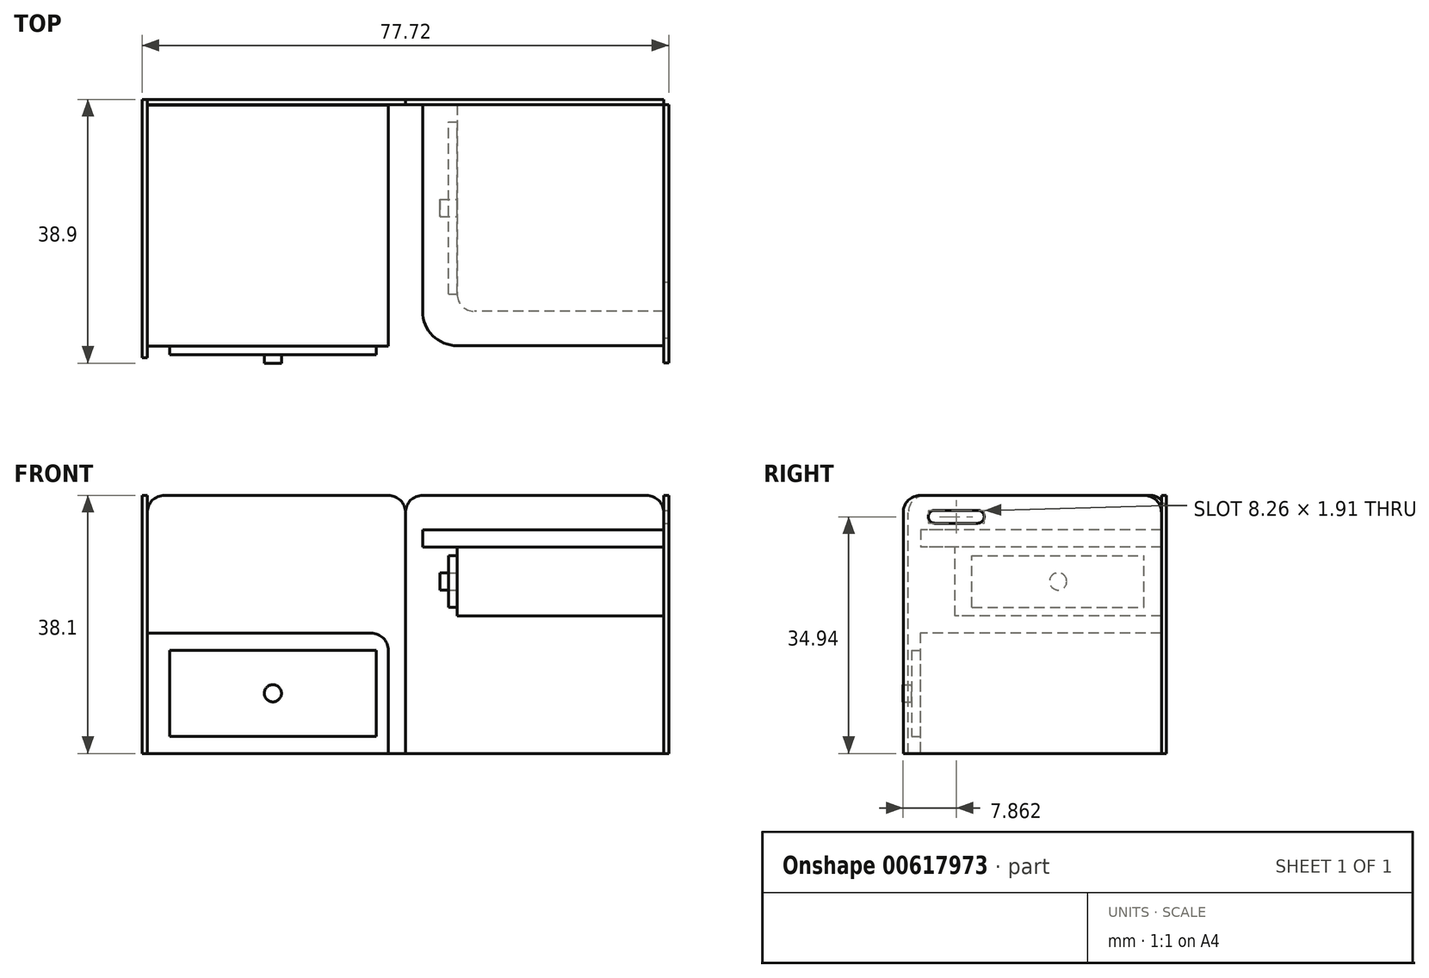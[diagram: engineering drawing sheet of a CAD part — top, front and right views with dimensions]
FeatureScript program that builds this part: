
annotation { "Feature Type Name" : "Feature", "Feature Type Description" : "" }
export const myFeature = defineFeature(function(context is Context, id is Id, definition is map)
    precondition{}
    {
        {
            var Q0;
            Q0=qCreatedBy(makeId("Right.planeOp"),FACE);
            var sketch = newSketch(context, id + "F0", { "sketchPlane" : qUnion([Q0])});
            skLineSegment(sketch, "E0.bottom", {"start": v(0, 0) * mm, "end": v(-38.1, 0) * mm});
            skLineSegment(sketch, "E0.top", {"start": v(0, 38.1) * mm, "end": v(-38.1, 38.1) * mm});
            skLineSegment(sketch, "E0.left", {"start": v(0, 0) * mm, "end": v(0, 38.1) * mm});
            skLineSegment(sketch, "E0.right", {"start": v(-38.1, 0) * mm, "end": v(-38.1, 38.1) * mm});
            skSolve(sketch);
        }
        {
            var Q0;
            Q0=qCreatedBy(makeId("Front.planeOp"),FACE);
            var sketch = newSketch(context, id + "F1", { "sketchPlane" : qUnion([Q0])});
            skLineSegment(sketch, "E1.0", {"start": v(0, 0) * mm, "end": v(0, 38.1) * mm});
            skLineSegment(sketch, "E2.bottom", {"start": v(0, 38.1) * mm, "end": v(38.1, 38.1) * mm});
            skLineSegment(sketch, "E2.top", {"start": v(0, 0) * mm, "end": v(38.1, 0) * mm});
            skLineSegment(sketch, "E2.left", {"start": v(0, 38.1) * mm, "end": v(0, 0) * mm});
            skLineSegment(sketch, "E2.right", {"start": v(38.1, 38.1) * mm, "end": v(38.1, 0) * mm});
            skLineSegment(sketch, "E3.bottom", {"start": v(38.1, 38.1) * mm, "end": v(76.2, 38.1) * mm});
            skLineSegment(sketch, "E3.top", {"start": v(38.1, 0) * mm, "end": v(76.2, 0) * mm});
            skLineSegment(sketch, "E3.right", {"start": v(76.2, 38.1) * mm, "end": v(76.2, 0) * mm});
            skSolve(sketch);
        }
        {
            var Q0;
            Q0=makeQuery(id+"F0.imprint","IMPRINT",FACE,{"disambiguationData":[TD([[makeQuery(id+"F0.imprint","IMPRINT",EDGE,{"derivedFrom":sQuery(id+"F0.wireOp",EDGE,"E0.bottom")}),-1.0]])]});
            extrude(context, id + "F2", {"entities" : qUnion([Q0]), "oppositeDirection" : true, "depth" : 0.76 * mm, "offsetDistance" : 25.4 * mm});
        }
        {
            var Q0;
            Q0=makeQuery(id+"F1.imprint","IMPRINT",FACE,{"disambiguationData":[TD([[makeQuery(id+"F1.imprint","IMPRINT",EDGE,{"derivedFrom":sQuery(id+"F1.wireOp",EDGE,"E2.bottom")}),-1.0]])]});
            extrude(context, id + "F3", {"entities" : qUnion([Q0]), "depth" : 0.76 * mm, "offsetDistance" : 25.4 * mm});
        }
        {
            var Q0;
            Q0=qCreatedBy(makeId("Top.planeOp"),FACE);
            var sketch = newSketch(context, id + "F4", { "sketchPlane" : qUnion([Q0])});
            skPoint(sketch, "E4.0", {"position": v(0, -0.8) * mm});
            skLineSegment(sketch, "E5.bottom", {"start": v(0, -0.8) * mm, "end": v(35.56, -0.8) * mm});
            skLineSegment(sketch, "E5.top", {"start": v(0, -36.36) * mm, "end": v(35.56, -36.36) * mm});
            skLineSegment(sketch, "E5.left", {"start": v(0, -0.8) * mm, "end": v(0, -36.36) * mm});
            skLineSegment(sketch, "E5.right", {"start": v(35.56, -0.8) * mm, "end": v(35.56, -36.36) * mm});
            skSolve(sketch);
        }
        {
            var Q0;
            Q0=makeQuery(id+"F4.imprint","IMPRINT",FACE,{"disambiguationData":[TD([[makeQuery(id+"F4.imprint","IMPRINT",EDGE,{"derivedFrom":sQuery(id+"F4.wireOp",EDGE,"E5.bottom")}),-1.0]])]});
            extrude(context, id + "F5", {"entities" : qUnion([Q0]), "depth" : 17.78 * mm});
        }
        {
            var Q0;
            Q0=makeQuery(id+"F5.opExtrude","CAP_FACE",FACE,{"disambiguationData":[OSD([sQuery(id+"F4.wireOp",EDGE,"E5.bottom"),sQuery(id+"F4.wireOp",EDGE,"E5.top"),sQuery(id+"F4.wireOp",EDGE,"E5.left"),sQuery(id+"F4.wireOp",EDGE,"E5.right")])],"isStart":false});
            cPlane(context, id + "F6", {"entities" : qUnion([Q0]), "cplaneType" : CPlaneType.OFFSET, "offset" : 12.7 * mm, "width" : 152.4 * mm, "height" : 152.4 * mm});
        }
        {
            var Q0;
            Q0=qCreatedBy(id+"F6.planeOp",FACE);
            var sketch = newSketch(context, id + "F7", { "sketchPlane" : qUnion([Q0])});
            skLineSegment(sketch, "E6.bottom", {"start": v(76.2, -0.76) * mm, "end": v(40.64, -0.76) * mm});
            skLineSegment(sketch, "E6.top", {"start": v(76.2, -36.32) * mm, "end": v(40.64, -36.32) * mm});
            skLineSegment(sketch, "E6.left", {"start": v(76.2, -0.76) * mm, "end": v(76.2, -36.32) * mm});
            skLineSegment(sketch, "E6.right", {"start": v(40.64, -0.76) * mm, "end": v(40.64, -36.32) * mm});
            skSolve(sketch);
        }
        {
            var Q0;
            Q0=qCreatedBy(id+"F6.planeOp",FACE);
            var sketch = newSketch(context, id + "F8", { "sketchPlane" : qUnion([Q0])});
            skLineSegment(sketch, "E7.bottom", {"start": v(76.2, -0.76) * mm, "end": v(45.72, -0.76) * mm});
            skLineSegment(sketch, "E7.top", {"start": v(76.2, -31.24) * mm, "end": v(45.72, -31.24) * mm});
            skLineSegment(sketch, "E7.left", {"start": v(76.2, -0.76) * mm, "end": v(76.2, -31.24) * mm});
            skLineSegment(sketch, "E7.right", {"start": v(45.72, -0.76) * mm, "end": v(45.72, -31.24) * mm});
            skSolve(sketch);
        }
        {
            var Q0;
            Q0=makeQuery(id+"F8.imprint","IMPRINT",FACE,{"disambiguationData":[TD([[makeQuery(id+"F8.imprint","IMPRINT",EDGE,{"derivedFrom":sQuery(id+"F8.wireOp",EDGE,"E7.bottom")}),1.0]])]});
            extrude(context, id + "F9", {"entities" : qUnion([Q0]), "oppositeDirection" : true, "depth" : 10.16 * mm});
        }
        {
            var Q0;
            Q0=qSketchRegion(id+"F7",true);
            extrude(context, id + "F10", {"entities" : qUnion([Q0]), "depth" : 2.54 * mm});
        }
        {
            var Q0;
            Q0=makeQuery(id+"F5.opExtrude","SWEPT_FACE",FACE,{"disambiguationData":[OSD([sQuery(id+"F4.wireOp",EDGE,"E5.top")])]});
            var sketch = newSketch(context, id + "F11", { "sketchPlane" : qUnion([Q0])});
            skLineSegment(sketch, "E8.0", {"start": v(35.56, 17.78) * mm, "end": v(35.56, 0) * mm});
            skLineSegment(sketch, "E9.0.2", {"start": v(35.56, 17.78) * mm, "end": v(0, 17.78) * mm});
            skLineSegment(sketch, "E9.0.3", {"start": v(0, 17.78) * mm, "end": v(0, 0) * mm});
            skLineSegment(sketch, "E10.bottom", {"start": v(33.78, 15.24) * mm, "end": v(3.3, 15.24) * mm});
            skLineSegment(sketch, "E10.top", {"start": v(33.78, 2.54) * mm, "end": v(3.3, 2.54) * mm});
            skLineSegment(sketch, "E10.left", {"start": v(33.78, 15.24) * mm, "end": v(33.78, 2.54) * mm});
            skLineSegment(sketch, "E10.right", {"start": v(3.3, 15.24) * mm, "end": v(3.3, 2.54) * mm});
            skPoint(sketch, "E10.middle", {"position": v(18.54, 8.9) * mm});
            skSolve(sketch);
        }
        {
            var Q0;
            Q0=makeQuery(id+"F11.imprint","IMPRINT",FACE,{"disambiguationData":[TD([[makeQuery(id+"F11.imprint","IMPRINT",EDGE,{"derivedFrom":sQuery(id+"F11.wireOp",EDGE,"E10.bottom")}),1.0]])]});
            extrude(context, id + "F12", {"entities" : qUnion([Q0]), "depth" : 1.27 * mm});
        }
        {
            var Q0;
            Q0=makeQuery(id+"F12.opExtrude","CAP_FACE",FACE,{"disambiguationData":[OSD([sQuery(id+"F11.wireOp",EDGE,"E10.bottom"),sQuery(id+"F11.wireOp",EDGE,"E10.top"),sQuery(id+"F11.wireOp",EDGE,"E10.left"),sQuery(id+"F11.wireOp",EDGE,"E10.right")])],"isStart":false});
            var sketch = newSketch(context, id + "F13", { "sketchPlane" : qUnion([Q0])});
            skCircle(sketch, "E11", {"center": v(18.54, 8.89) * mm, "radius": 1.27 * mm});
            skSolve(sketch);
        }
        {
            var Q0;
            Q0=makeQuery(id+"F13.imprint","IMPRINT",FACE,{"disambiguationData":[TD([[makeQuery(id+"F13.imprint","IMPRINT",EDGE,{"derivedFrom":sQuery(id+"F13.wireOp",EDGE,"E11")}),1.0]])]});
            extrude(context, id + "F14", {"entities" : qUnion([Q0]), "depth" : 1.27 * mm});
        }
        {
            var Q0;
            Q0=makeQuery(id+"F9.opExtrude","SWEPT_FACE",FACE,{"disambiguationData":[OSD([sQuery(id+"F8.wireOp",EDGE,"E7.right")])]});
            var sketch = newSketch(context, id + "F15", { "sketchPlane" : qUnion([Q0])});
            skLineSegment(sketch, "E12.bottom", {"start": v(28.7, 21.59) * mm, "end": v(3.3, 21.59) * mm});
            skLineSegment(sketch, "E12.top", {"start": v(28.7, 29.2) * mm, "end": v(3.3, 29.2) * mm});
            skLineSegment(sketch, "E12.left", {"start": v(28.7, 21.59) * mm, "end": v(28.7, 29.2) * mm});
            skLineSegment(sketch, "E12.right", {"start": v(3.3, 21.59) * mm, "end": v(3.3, 29.2) * mm});
            skPoint(sketch, "E12.middle", {"position": v(16, 25.4) * mm});
            skSolve(sketch);
        }
        {
            var Q0;
            Q0=makeQuery(id+"F15.imprint","IMPRINT",FACE,{"disambiguationData":[TD([[makeQuery(id+"F15.imprint","IMPRINT",EDGE,{"derivedFrom":sQuery(id+"F15.wireOp",EDGE,"E12.bottom")}),1.0]])]});
            var sketch = newSketch(context, id + "F16", { "sketchPlane" : qUnion([Q0])});
            skCircle(sketch, "E13", {"center": v(16, 25.4) * mm, "radius": 1.27 * mm});
            skSolve(sketch);
        }
        {
            var Q0;
            Q0=makeQuery(id+"F16.imprint","IMPRINT",FACE,{"disambiguationData":[TD([[makeQuery(id+"F16.imprint","IMPRINT",EDGE,{"derivedFrom":sQuery(id+"F16.wireOp",EDGE,"E13")}),1.0]])]});
            extrude(context, id + "F17", {"entities" : qUnion([Q0]), "depth" : 2.54 * mm});
        }
        {
            var Q0;
            Q0=makeQuery(id+"F15.imprint","IMPRINT",FACE,{"disambiguationData":[TD([[makeQuery(id+"F15.imprint","IMPRINT",EDGE,{"derivedFrom":sQuery(id+"F15.wireOp",EDGE,"E12.bottom")}),-1.0]])]});
            extrude(context, id + "F18", {"entities" : qUnion([Q0]), "depth" : 1.27 * mm});
        }
        {
            var Q0;
            Q0=makeQuery(id+"F2.opExtrude","SWEPT_EDGE",EDGE,{"disambiguationData":[OSD([sQuery(id+"F0.wireOp",EDGE,"E0.top"),sQuery(id+"F0.wireOp",EDGE,"E0.right")])]});
            var Q1;
            Q1=makeQuery(id+"F2.opExtrude","SWEPT_EDGE",EDGE,{"disambiguationData":[OSD([sQuery(id+"F0.wireOp",EDGE,"E0.top"),sQuery(id+"F0.wireOp",EDGE,"E0.left")])]});
            var Q2;
            Q2=makeQuery(id+"F3.opExtrude","SWEPT_EDGE",EDGE,{"disambiguationData":[OSD([sQuery(id+"FI0QwBpxzJms6q6_1.wireOp",EDGE,"EPlBsMqQ-QzQ8-VdCQ-xvKd-hzmvY7jMW2L1.bottom"),sQuery(id+"FI0QwBpxzJms6q6_1.wireOp",EDGE,"EPlBsMqQ-QzQ8-VdCQ-xvKd-hzmvY7jMW2L1.right")])]});
            var Q3;
            Q3=makeQuery(id+"FcK2yJQiMoCniT7_2.opExtrude","SWEPT_EDGE",EDGE,{"disambiguationData":[OSD([sQuery(id+"FKOlXeHhfTV6Gp4_1.wireOp",EDGE,"gBm9quYi-xdeT-jJYe-hTa2-NPwO5Kq9pGmv.bottom"),sQuery(id+"FKOlXeHhfTV6Gp4_1.wireOp",EDGE,"gBm9quYi-xdeT-jJYe-hTa2-NPwO5Kq9pGmv.right")])]});
            var Q4;
            Q4=makeQuery(id+"FcK2yJQiMoCniT7_2.opExtrude","SWEPT_EDGE",EDGE,{"disambiguationData":[OSD([sQuery(id+"FKOlXeHhfTV6Gp4_1.wireOp",EDGE,"gBm9quYi-xdeT-jJYe-hTa2-NPwO5Kq9pGmv.bottom"),sQuery(id+"FKOlXeHhfTV6Gp4_1.wireOp",EDGE,"gBm9quYi-xdeT-jJYe-hTa2-NPwO5Kq9pGmv.left")])]});
            var Q5;
            Q5=makeQuery(id+"F3.opExtrude","SWEPT_EDGE",EDGE,{"disambiguationData":[OSD([sQuery(id+"F1.wireOp",EDGE,"E3.bottom"),sQuery(id+"F1.wireOp",EDGE,"E3.right")])]});
            var Q6;
            Q6=makeQuery(id+"F3.opExtrude","SWEPT_EDGE",EDGE,{"disambiguationData":[OSD([sQuery(id+"F1.wireOp",EDGE,"E2.bottom"),sQuery(id+"F1.wireOp",EDGE,"E2.left")])]});
            fillet(context, id + "F19", {"entities" : qUnion([Q0, Q1, Q2, Q3, Q4, Q5, Q6]), "radius" : 2.54 * mm, "tangentPropagation" : true, "allowEdgeOverflow" : false});
        }
        {
            var Q0;
            Q0=makeQuery(id+"F10.opExtrude","SWEPT_EDGE",EDGE,{"disambiguationData":[OSD([sQuery(id+"F7.wireOp",EDGE,"E6.top"),sQuery(id+"F7.wireOp",EDGE,"E6.right")])]});
            fillet(context, id + "F20", {"entities" : qUnion([Q0]), "radius" : 5.08 * mm, "tangentPropagation" : true, "allowEdgeOverflow" : false});
        }
        {
            var Q0;
            Q0=makeQuery(id+"F9.opExtrude","SWEPT_EDGE",EDGE,{"disambiguationData":[OSD([sQuery(id+"F8.wireOp",EDGE,"E7.top"),sQuery(id+"F8.wireOp",EDGE,"E7.right")])]});
            var Q1;
            Q1=makeQuery(id+"F5.opExtrude","CAP_EDGE",EDGE,{"disambiguationData":[OSD([sQuery(id+"F4.wireOp",EDGE,"E5.right")])],"isStart":false});
            fillet(context, id + "F21", {"entities" : qUnion([Q0, Q1]), "radius" : 2.54 * mm, "tangentPropagation" : true, "allowEdgeOverflow" : false});
        }
        {
            var Q0;
            Q0=makeQuery(id+"F2.opExtrude","CAP_FACE",FACE,{"disambiguationData":[OSD([sQuery(id+"F0.wireOp",EDGE,"E0.bottom"),sQuery(id+"F0.wireOp",EDGE,"E0.top"),sQuery(id+"F0.wireOp",EDGE,"E0.left"),sQuery(id+"F0.wireOp",EDGE,"E0.right")])],"isStart":true});
            var sketch = newSketch(context, id + "F22", { "sketchPlane" : qUnion([Q0])});
            skLineSegment(sketch, "E14.left", {"start": v(33.38, 34.48) * mm, "end": v(33.38, 28.13) * mm});
            skLineSegment(sketch, "E14.right", {"start": v(35.28, 34.48) * mm, "end": v(35.28, 28.13) * mm});
            skArc(sketch, "E15", {"start": v(35.28, 34.48) * mm, "mid": v(34.33, 35.43) * mm, "end": v(33.38, 34.48) * mm});
            skArc(sketch, "E16", {"start": v(33.38, 28.13) * mm, "mid": v(34.33, 27.18) * mm, "end": v(35.28, 28.13) * mm});
            skSolve(sketch);
        }
        {
            var Q0;
            Q0=qSketchRegion(id+"F22",true);
            extrude(context, id + "F23", {"entities" : qUnion([Q0]), "operationType" : NewBodyOperationType.REMOVE, "oppositeDirection" : true, "depth" : 12.7 * mm, "offsetDistance" : 25.4 * mm});
        }
        {
            var Q0;
            Q0=makeQuery(id+"F1.imprint","IMPRINT",FACE,{"disambiguationData":[TD([[makeQuery(id+"F1.imprint","IMPRINT",EDGE,{"derivedFrom":sQuery(id+"F1.wireOp",EDGE,"E3.bottom")}),-1.0]])]});
            extrude(context, id + "F24", {"entities" : qUnion([Q0]), "depth" : 0.76 * mm, "offsetDistance" : 25.4 * mm});
        }
        {
            var Q0;
            Q0=qCreatedBy(makeId("Right.planeOp"),FACE);
            cPlane(context, id + "F25", {"entities" : qUnion([Q0]), "cplaneType" : CPlaneType.OFFSET, "offset" : 76.2 * mm, "width" : 152.4 * mm, "height" : 152.4 * mm});
        }
        {
            var Q0;
            Q0=qCreatedBy(id+"F25.planeOp",FACE);
            var sketch = newSketch(context, id + "F26", { "sketchPlane" : qUnion([Q0])});
            skLineSegment(sketch, "E17.bottom", {"start": v(-0.76, 38.1) * mm, "end": v(-38.86, 38.1) * mm});
            skLineSegment(sketch, "E17.top", {"start": v(-0.76, 0) * mm, "end": v(-38.86, 0) * mm});
            skLineSegment(sketch, "E17.left", {"start": v(-0.76, 38.1) * mm, "end": v(-0.76, 0) * mm});
            skLineSegment(sketch, "E17.right", {"start": v(-38.86, 38.1) * mm, "end": v(-38.86, 0) * mm});
            skSolve(sketch);
        }
        {
            var Q0;
            Q0=qSketchRegion(id+"F26",true);
            extrude(context, id + "F27", {"entities" : qUnion([Q0]), "depth" : 0.76 * mm, "offsetDistance" : 25.4 * mm});
        }
        {
            var Q0;
            Q0=makeQuery(id+"F27.opExtrude","CAP_FACE",FACE,{"disambiguationData":[OSD([sQuery(id+"F26.wireOp",EDGE,"E17.bottom"),sQuery(id+"F26.wireOp",EDGE,"E17.top"),sQuery(id+"F26.wireOp",EDGE,"E17.left"),sQuery(id+"F26.wireOp",EDGE,"E17.right")])],"isStart":false});
            var sketch = newSketch(context, id + "F28", { "sketchPlane" : qUnion([Q0])});
            skLineSegment(sketch, "E18.bottom", {"start": v(-34.21, 35.9) * mm, "end": v(-27.86, 35.9) * mm});
            skLineSegment(sketch, "E18.top", {"start": v(-34.21, 33.99) * mm, "end": v(-27.86, 33.99) * mm});
            skArc(sketch, "E19", {"start": v(-27.86, 33.99) * mm, "mid": v(-26.91, 34.94) * mm, "end": v(-27.86, 35.9) * mm});
            skArc(sketch, "E20", {"start": v(-34.21, 35.9) * mm, "mid": v(-35.17, 34.94) * mm, "end": v(-34.21, 33.99) * mm});
            skSolve(sketch);
        }
        {
            var Q0;
            Q0=makeQuery(id+"F28.imprint","IMPRINT",FACE,{"disambiguationData":[TD([[makeQuery(id+"F28.imprint","IMPRINT",EDGE,{"derivedFrom":sQuery(id+"F28.wireOp",EDGE,"E18.bottom")}),-1.0]])]});
            extrude(context, id + "F29", {"entities" : qUnion([Q0]), "operationType" : NewBodyOperationType.REMOVE, "oppositeDirection" : true, "depth" : 12.7 * mm, "offsetDistance" : 25.4 * mm});
        }
        {
            var Q0;
            Q0=makeQuery(id+"F24.opExtrude","SWEPT_EDGE",EDGE,{"disambiguationData":[OSD([sQuery(id+"F1.wireOp",EDGE,"E3.bottom"),sQuery(id+"F1.wireOp",EDGE,"E3.right")])]});
            var Q1;
            Q1=makeQuery(id+"F27.opExtrude","SWEPT_EDGE",EDGE,{"disambiguationData":[OSD([sQuery(id+"F26.wireOp",EDGE,"E17.bottom"),sQuery(id+"F26.wireOp",EDGE,"E17.left")])]});
            var Q2;
            Q2=makeQuery(id+"F24.opExtrude","SWEPT_EDGE",EDGE,{"disambiguationData":[OSD([sQuery(id+"F1.wireOp",EDGE,"E2.bottom"),sQuery(id+"F1.wireOp",EDGE,"E3.bottom"),sQuery(id+"F1.wireOp",EDGE,"E2.right")])]});
            var Q3;
            Q3=makeQuery(id+"F27.opExtrude","SWEPT_EDGE",EDGE,{"disambiguationData":[OSD([sQuery(id+"F26.wireOp",EDGE,"E17.bottom"),sQuery(id+"F26.wireOp",EDGE,"E17.right")])]});
            fillet(context, id + "F30", {"entities" : qUnion([Q0, Q1, Q2, Q3]), "radius" : 2.54 * mm, "tangentPropagation" : true, "allowEdgeOverflow" : false});
        }
    });
